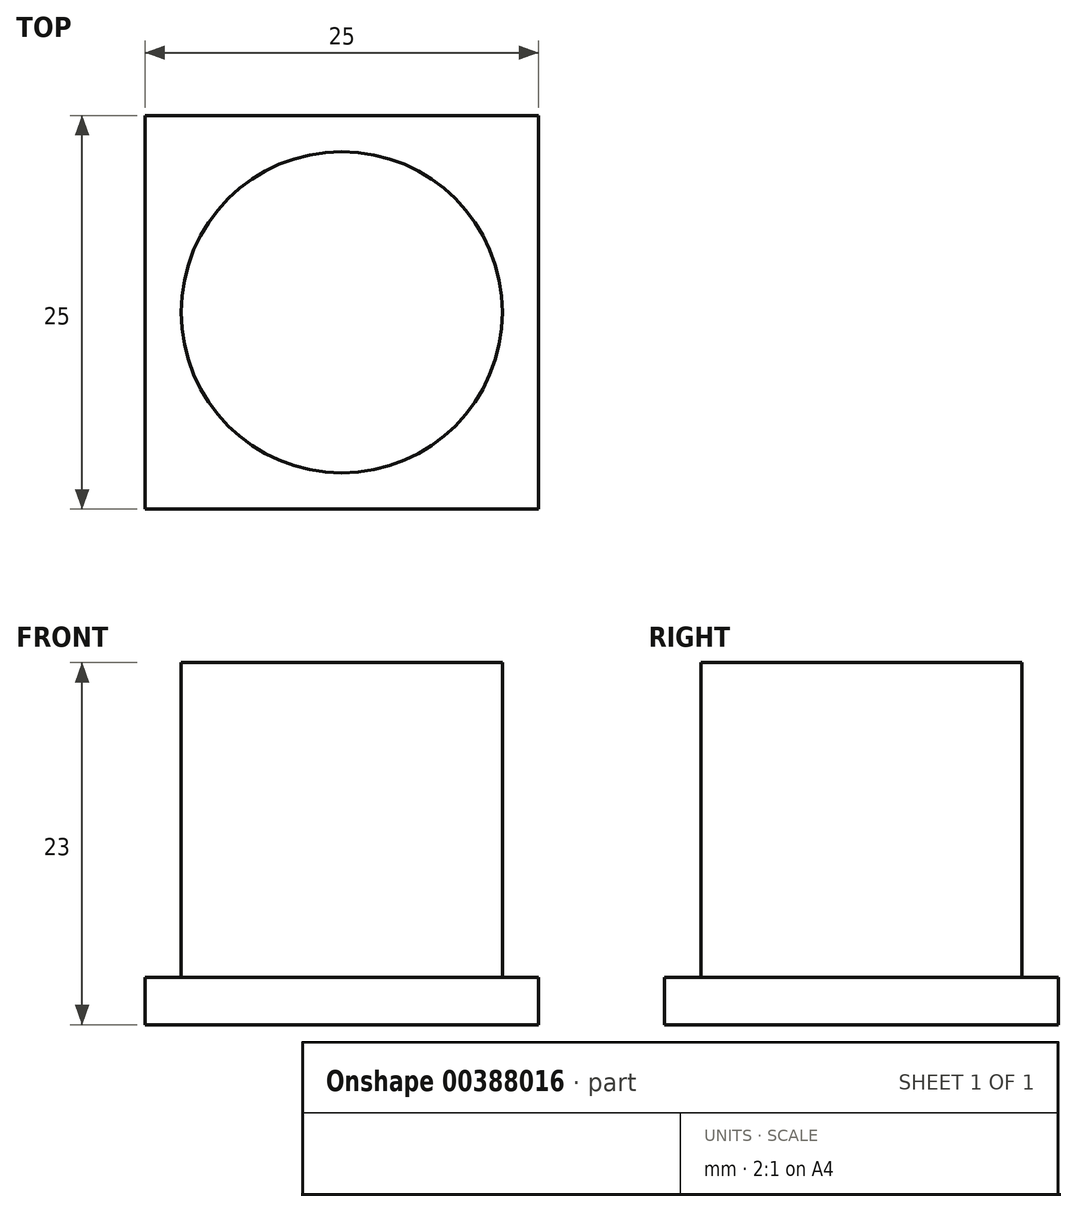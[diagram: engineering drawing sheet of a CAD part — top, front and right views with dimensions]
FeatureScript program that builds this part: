
annotation { "Feature Type Name" : "Feature", "Feature Type Description" : "" }
export const myFeature = defineFeature(function(context is Context, id is Id, definition is map)
    precondition{}
    {
        {
            var Q0;
            Q0=qCreatedBy(makeId("Top.planeOp"),FACE);
            var sketch = newSketch(context, id + "F0", { "sketchPlane" : qUnion([Q0])});
            skLineSegment(sketch, "E0.bottom", {"start": v(-12.5, 12.5) * mm, "end": v(0, 12.5) * mm});
            skLineSegment(sketch, "E0.top", {"start": v(-12.5, -12.5) * mm, "end": v(12.5, -12.5) * mm});
            skLineSegment(sketch, "E0.left", {"start": v(-12.5, 12.5) * mm, "end": v(-12.5, 0) * mm});
            skLineSegment(sketch, "E0.right", {"start": v(12.5, 12.5) * mm, "end": v(12.5, -12.5) * mm});
            skLineSegment(sketch, "E1", {"start": v(0, 12.5) * mm, "end": v(12.5, 12.5) * mm});
            skLineSegment(sketch, "E2", {"start": v(-12.5, 0) * mm, "end": v(-12.5, -12.5) * mm});
            skSolve(sketch);
        }
        {
            var Q0;
            Q0=makeQuery(id+"F0.imprint","IMPRINT",FACE,{"disambiguationData":[TD([[makeQuery(id+"F0.imprint","IMPRINT",EDGE,{"derivedFrom":sQuery(id+"F0.wireOp",EDGE,"E0.bottom")}),-1.0]])]});
            extrude(context, id + "F1", {"entities" : qUnion([Q0]), "depth" : 3 * mm});
        }
        {
            var Q0;
            Q0=makeQuery(id+"F1.opExtrude","CAP_FACE",FACE,{"disambiguationData":[OSD([sQuery(id+"F0.wireOp",EDGE,"E0.bottom"),sQuery(id+"F0.wireOp",EDGE,"E0.top"),sQuery(id+"F0.wireOp",EDGE,"E0.left"),sQuery(id+"F0.wireOp",EDGE,"E0.right"),sQuery(id+"F0.wireOp",EDGE,"E1"),sQuery(id+"F0.wireOp",EDGE,"E2")])],"isStart":false});
            var sketch = newSketch(context, id + "F2", { "sketchPlane" : qUnion([Q0])});
            skCircle(sketch, "E3", {"center": v(0, 0) * mm, "radius": 10.2 * mm});
            skSolve(sketch);
        }
        {
            var Q0;
            Q0=makeQuery(id+"F2.imprint","IMPRINT",FACE,{"disambiguationData":[TD([[makeQuery(id+"F2.imprint","IMPRINT",EDGE,{"derivedFrom":sQuery(id+"F2.wireOp",EDGE,"E3")}),1.0]])]});
            extrude(context, id + "F3", {"entities" : qUnion([Q0]), "operationType" : NewBodyOperationType.ADD, "depth" : 20 * mm});
        }
    });
